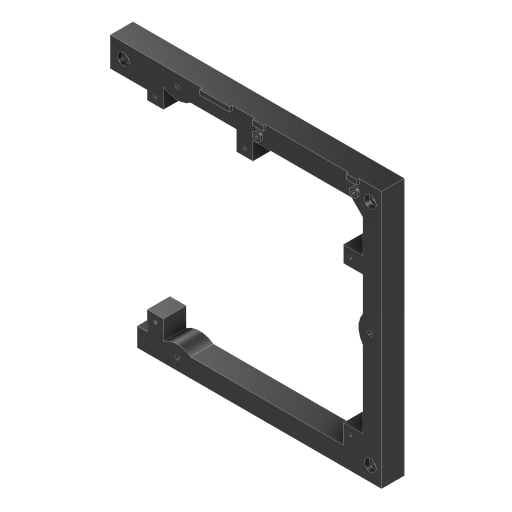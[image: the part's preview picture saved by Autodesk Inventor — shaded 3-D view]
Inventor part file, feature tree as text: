
AUTODESK INVENTOR PART (.ipt)
format: ipt  version: 2023 (Build 270158000, 158)  size: 808,960 bytes
history: native  units: mm
features: sketch x10, projected_geometry x10, extrude x5, hole x5, other x1, chamfer x1
ambient origin geometry x8: Origin, YZ Plane, XZ Plane, XY Plane, X Axis, Y Axis, Z Axis, Center Point
bodies: Body1 (feature_tree)
feature tree (32):
  other  "Těleso1"
  extrude  "Vysunutí1"  Depth=158.5mm
  chamfer  "Zkosení1"  Distance=11.5mm
  extrude  "Vysunutí2"  Depth=18.0mm
  hole  "Díra2"  [1 undecoded]
  extrude  "Vysunutí3"  Depth=130.0mm
  hole  "Díra3"  [1 undecoded]
  hole  "Díra4"  [1 undecoded]
  hole  "Díra5"  [1 undecoded]
  extrude  "Vysunutí4"  Depth=40.0mm
  extrude  "Vysunutí5"  Depth=65.0mm
  hole  "Díra6"  [1 undecoded]
  sketch  "Náčrt1"
  sketch  "Náčrt2"
  projected_geometry  "Promítnutá smyčka1"
  sketch  "Náčrt3"
  projected_geometry  "Promítnutá smyčka2"
  projected_geometry  "Promítnutá smyčka3"
  sketch  "Náčrt4"
  projected_geometry  "Promítnutá smyčka4"
  sketch  "Náčrt5"
  projected_geometry  "Promítnutá smyčka5"
  sketch  "Náčrt6"
  projected_geometry  "Promítnutá smyčka6"
  sketch  "Náčrt7"
  projected_geometry  "Promítnutá smyčka7"
  sketch  "Náčrt8"
  projected_geometry  "Promítnutá smyčka8"
  sketch  "Náčrt9"
  projected_geometry  "Promítnutá smyčka9"
  sketch  "Náčrt10"
  projected_geometry  "Promítnutá smyčka10"
note: 5 required parameter values undecoded (feature->parameter linkage not recoverable at this tier; creation-order binding heuristic only, values carry confidence <= 0.55)
